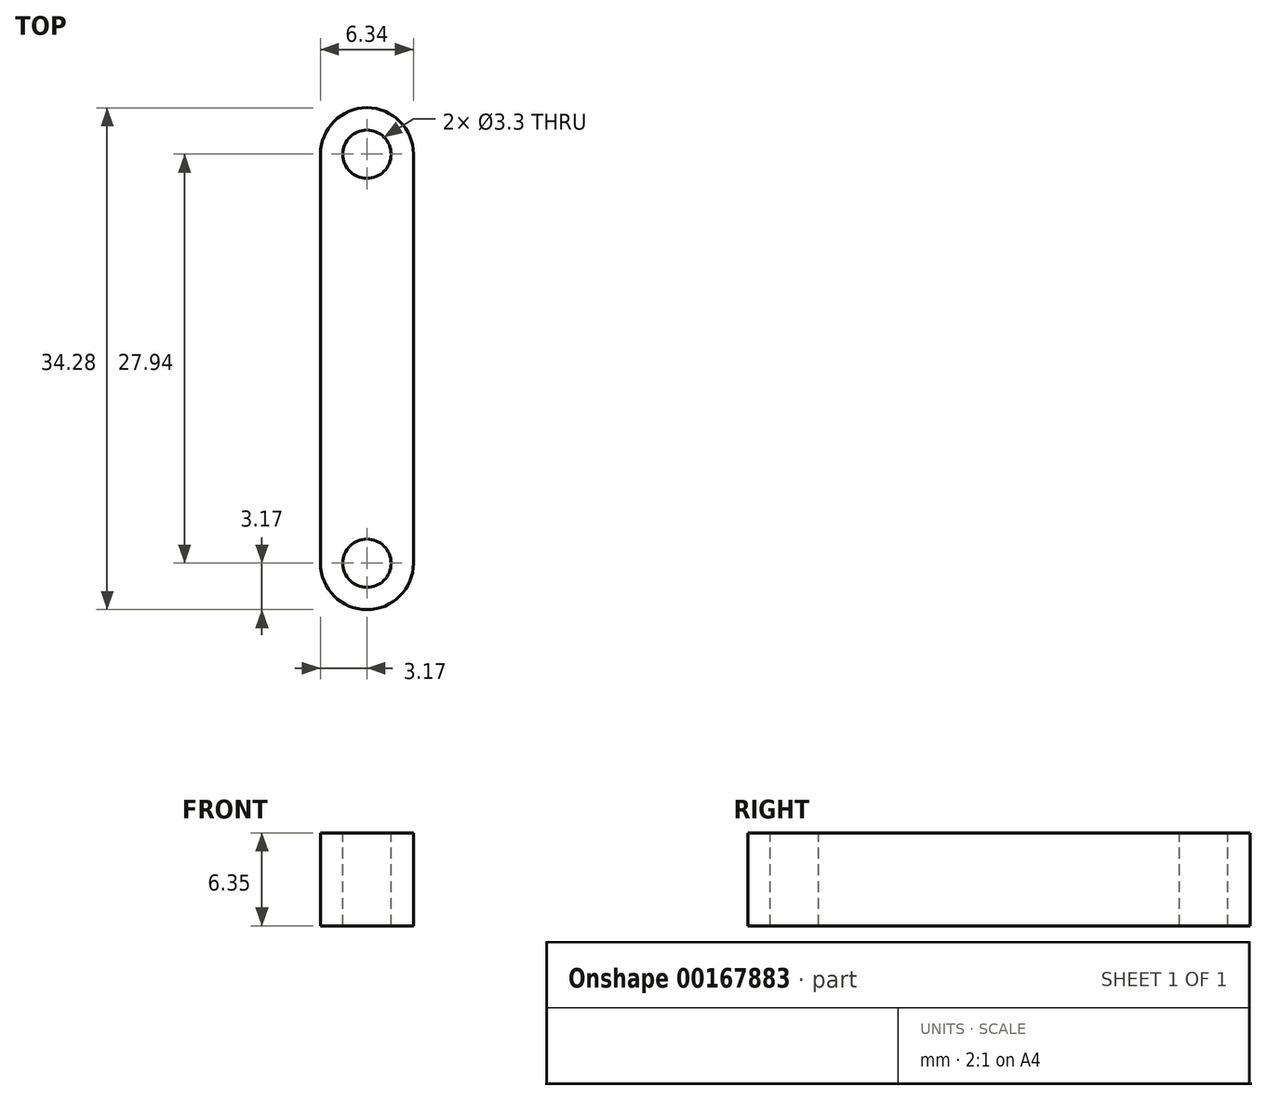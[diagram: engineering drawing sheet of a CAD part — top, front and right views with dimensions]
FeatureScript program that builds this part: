
annotation { "Feature Type Name" : "Feature", "Feature Type Description" : "" }
export const myFeature = defineFeature(function(context is Context, id is Id, definition is map)
    precondition{}
    {
        {
            var Q0;
            Q0=qCreatedBy(makeId("Top.planeOp"),FACE);
            var sketch = newSketch(context, id + "F0", { "sketchPlane" : qUnion([Q0])});
            skLineSegment(sketch, "E0.bottom", {"start": v(3.17, -17.15) * mm, "end": v(-3.18, -17.15) * mm});
            skLineSegment(sketch, "E0.top", {"start": v(3.17, 17.15) * mm, "end": v(-3.18, 17.15) * mm});
            skLineSegment(sketch, "E0.left", {"start": v(3.17, -17.15) * mm, "end": v(3.17, 17.15) * mm});
            skLineSegment(sketch, "E0.right", {"start": v(-3.18, -17.15) * mm, "end": v(-3.18, 17.15) * mm});
            skPoint(sketch, "E0.middle", {"position": v(0, 0) * mm});
            skSolve(sketch);
        }
        {
            var Q0;
            Q0 = qSketchRegion(id + "F0", true);
            extrude(context, id + "F1", {"entities" : qUnion([Q0]), "depth" : 6.35 * mm});
        }
        {
            var Q0;
            Q0=makeQuery(id+"F1.opExtrude","SWEPT_EDGE",EDGE,{"disambiguationData":[OSD([sQuery(id+"F0.wireOp",EDGE,"E0.top"),sQuery(id+"F0.wireOp",EDGE,"E0.left")])]});
            var Q1;
            Q1=makeQuery(id+"F1.opExtrude","SWEPT_EDGE",EDGE,{"disambiguationData":[OSD([sQuery(id+"F0.wireOp",EDGE,"E0.top"),sQuery(id+"F0.wireOp",EDGE,"E0.right")])]});
            var Q2;
            Q2=makeQuery(id+"F1.opExtrude","SWEPT_EDGE",EDGE,{"disambiguationData":[OSD([sQuery(id+"F0.wireOp",EDGE,"E0.bottom"),sQuery(id+"F0.wireOp",EDGE,"E0.left")])]});
            var Q3;
            Q3=makeQuery(id+"F1.opExtrude","SWEPT_EDGE",EDGE,{"disambiguationData":[OSD([sQuery(id+"F0.wireOp",EDGE,"E0.bottom"),sQuery(id+"F0.wireOp",EDGE,"E0.right")])]});
            fillet(context, id + "F2", {"entities" : qUnion([Q0, Q1, Q2, Q3]), "radius" : 3.17 * mm, "tangentPropagation" : true, "allowEdgeOverflow" : false});
        }
        {
            var Q0;
            Q0=makeQuery(id+"F1.opExtrude","CAP_FACE",FACE,{"disambiguationData":[OSD([sQuery(id+"F0.wireOp",EDGE,"E0.bottom"),sQuery(id+"F0.wireOp",EDGE,"E0.top"),sQuery(id+"F0.wireOp",EDGE,"E0.left"),sQuery(id+"F0.wireOp",EDGE,"E0.right")])],"isStart":false});
            var sketch = newSketch(context, id + "F3", { "sketchPlane" : qUnion([Q0])});
            skCircle(sketch, "E1", {"center": v(0, -13.97) * mm, "radius": 1.65 * mm});
            skCircle(sketch, "E2", {"center": v(0, 13.97) * mm, "radius": 1.65 * mm});
            skSolve(sketch);
        }
        {
            var Q0;
            Q0 = qSketchRegion(id + "F3", true);
            var Q1;
            Q1=makeQuery(id+"F1.opExtrude","CAP_FACE",FACE,{"disambiguationData":[OSD([sQuery(id+"F0.wireOp",EDGE,"E0.bottom"),sQuery(id+"F0.wireOp",EDGE,"E0.top"),sQuery(id+"F0.wireOp",EDGE,"E0.left"),sQuery(id+"F0.wireOp",EDGE,"E0.right")])],"isStart":true});
            extrude(context, id + "F4", {"entities" : qUnion([Q0]), "operationType" : NewBodyOperationType.REMOVE, "endBound" : BoundingType.UP_TO_SURFACE, "oppositeDirection" : true, "endBoundEntityFace" : qUnion([Q1]), "depth" : 25.4 * mm});
        }
    });
